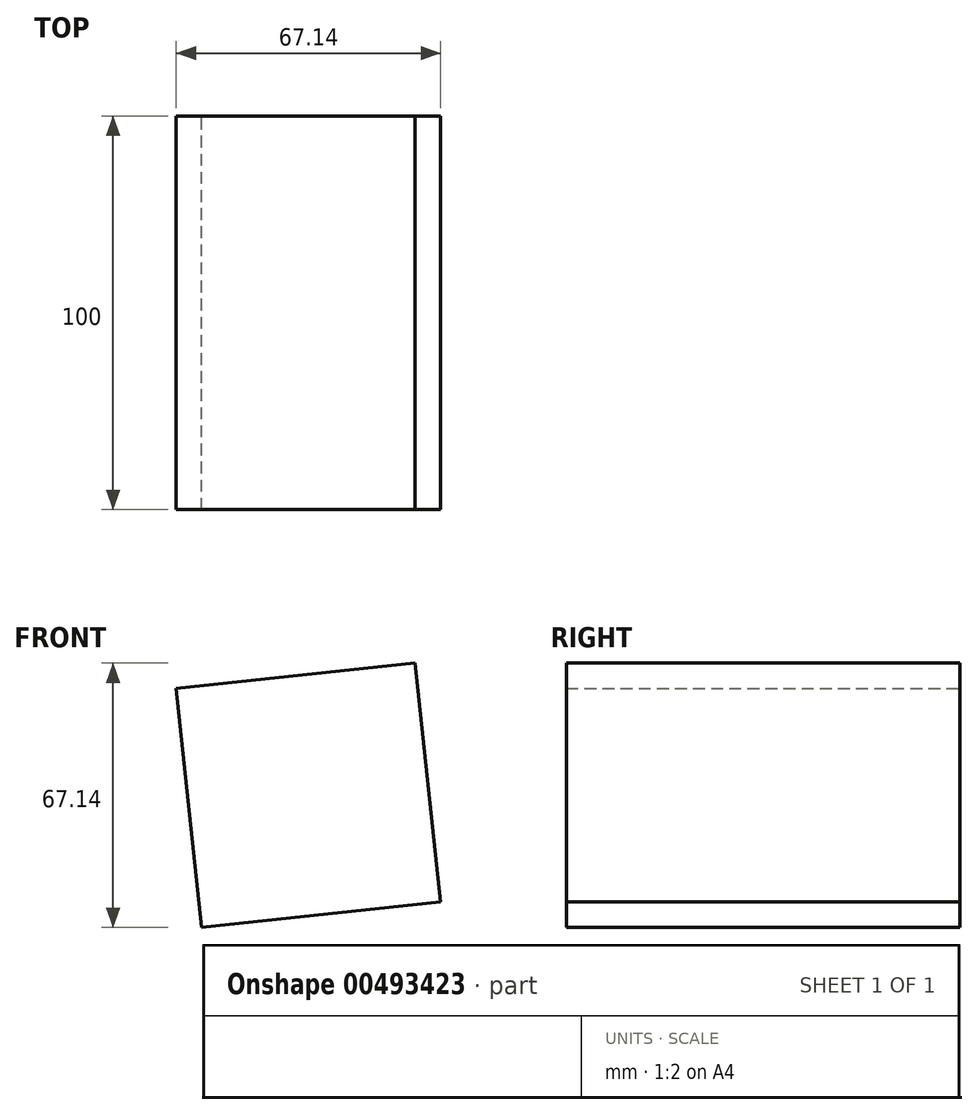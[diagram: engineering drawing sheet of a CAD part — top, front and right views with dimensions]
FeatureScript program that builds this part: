
annotation { "Feature Type Name" : "Feature", "Feature Type Description" : "" }
export const myFeature = defineFeature(function(context is Context, id is Id, definition is map)
    precondition{}
    {
        {
            var Q0;
            Q0=qCreatedBy(makeId("Front.planeOp"),FACE);
            var sketch = newSketch(context, id + "F0", { "sketchPlane" : qUnion([Q0])});
            skCircle(sketch, "E0.cCircle", {"center": v(0, 0) * mm, "radius": 43.15 * mm, "construction": true});
            skLineSegment(sketch, "E0.0", {"start": v(-33.57, 27.11) * mm, "end": v(27.11, 33.57) * mm});
            skLineSegment(sketch, "E0.1", {"start": v(27.11, 33.57) * mm, "end": v(33.57, -27.11) * mm});
            skLineSegment(sketch, "E0.2", {"start": v(33.57, -27.11) * mm, "end": v(-27.11, -33.57) * mm});
            skLineSegment(sketch, "E0.3", {"start": v(-27.11, -33.57) * mm, "end": v(-33.57, 27.11) * mm});
            skSolve(sketch);
        }
        {
            var Q0;
            Q0 = qSketchRegion(id + "F0", true);
            extrude(context, id + "F1", {"entities" : qUnion([Q0]), "endBound" : BoundingType.SYMMETRIC, "depth" : 100 * mm});
        }
    });
